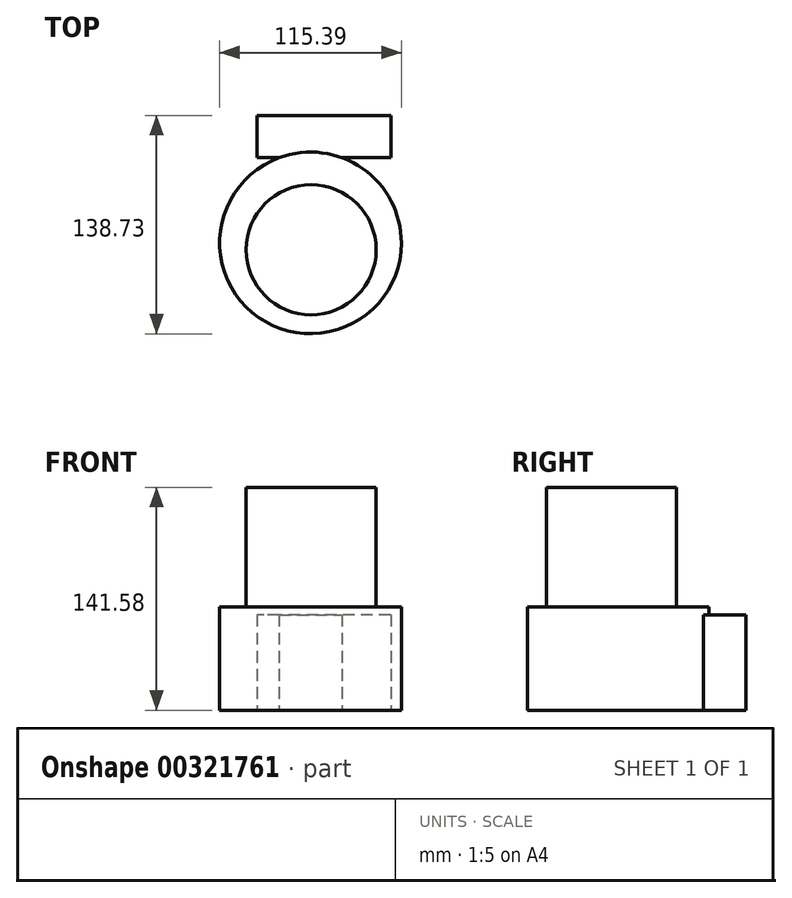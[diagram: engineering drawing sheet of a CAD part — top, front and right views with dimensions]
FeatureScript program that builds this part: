
annotation { "Feature Type Name" : "Feature", "Feature Type Description" : "" }
export const myFeature = defineFeature(function(context is Context, id is Id, definition is map)
    precondition{}
    {
        {
            var Q0;
            Q0=qCreatedBy(makeId("Top.planeOp"),FACE);
            var sketch = newSketch(context, id + "F0", { "sketchPlane" : qUnion([Q0])});
            skCircle(sketch, "E0", {"center": v(33.9, 64.87) * mm, "radius": 57.7 * mm});
            skSolve(sketch);
        }
        {
            var Q0;
            Q0 = qSketchRegion(id + "F0", true);
            extrude(context, id + "F1", {"entities" : qUnion([Q0]), "depth" : 65.48 * mm});
        }
        {
            var Q0;
            Q0=qCreatedBy(makeId("Top.planeOp"),FACE);
            var sketch = newSketch(context, id + "F2", { "sketchPlane" : qUnion([Q0])});
            skCircle(sketch, "E1", {"center": v(34.26, 60.52) * mm, "radius": 41.3 * mm});
            skSolve(sketch);
        }
        {
            var Q0;
            Q0 = qSketchRegion(id + "F2", true);
            extrude(context, id + "F3", {"entities" : qUnion([Q0]), "operationType" : NewBodyOperationType.ADD, "depth" : 141.58 * mm});
        }
        {
            var Q0;
            Q0=qCreatedBy(makeId("Right.planeOp"),FACE);
            var sketch = newSketch(context, id + "F4", { "sketchPlane" : qUnion([Q0])});
            skLineSegment(sketch, "E2.bottom", {"start": v(145.9, 60.64) * mm, "end": v(119.03, 60.64) * mm});
            skLineSegment(sketch, "E2.top", {"start": v(145.9, 0) * mm, "end": v(119.03, 0) * mm});
            skLineSegment(sketch, "E2.left", {"start": v(145.9, 60.64) * mm, "end": v(145.9, 0) * mm});
            skLineSegment(sketch, "E2.right", {"start": v(119.03, 60.64) * mm, "end": v(119.03, 0) * mm});
            skSolve(sketch);
        }
        {
            var Q0;
            Q0 = qSketchRegion(id + "F4", true);
            extrude(context, id + "F5", {"entities" : qUnion([Q0]), "operationType" : NewBodyOperationType.ADD, "depth" : 84.92 * mm});
        }
    });
